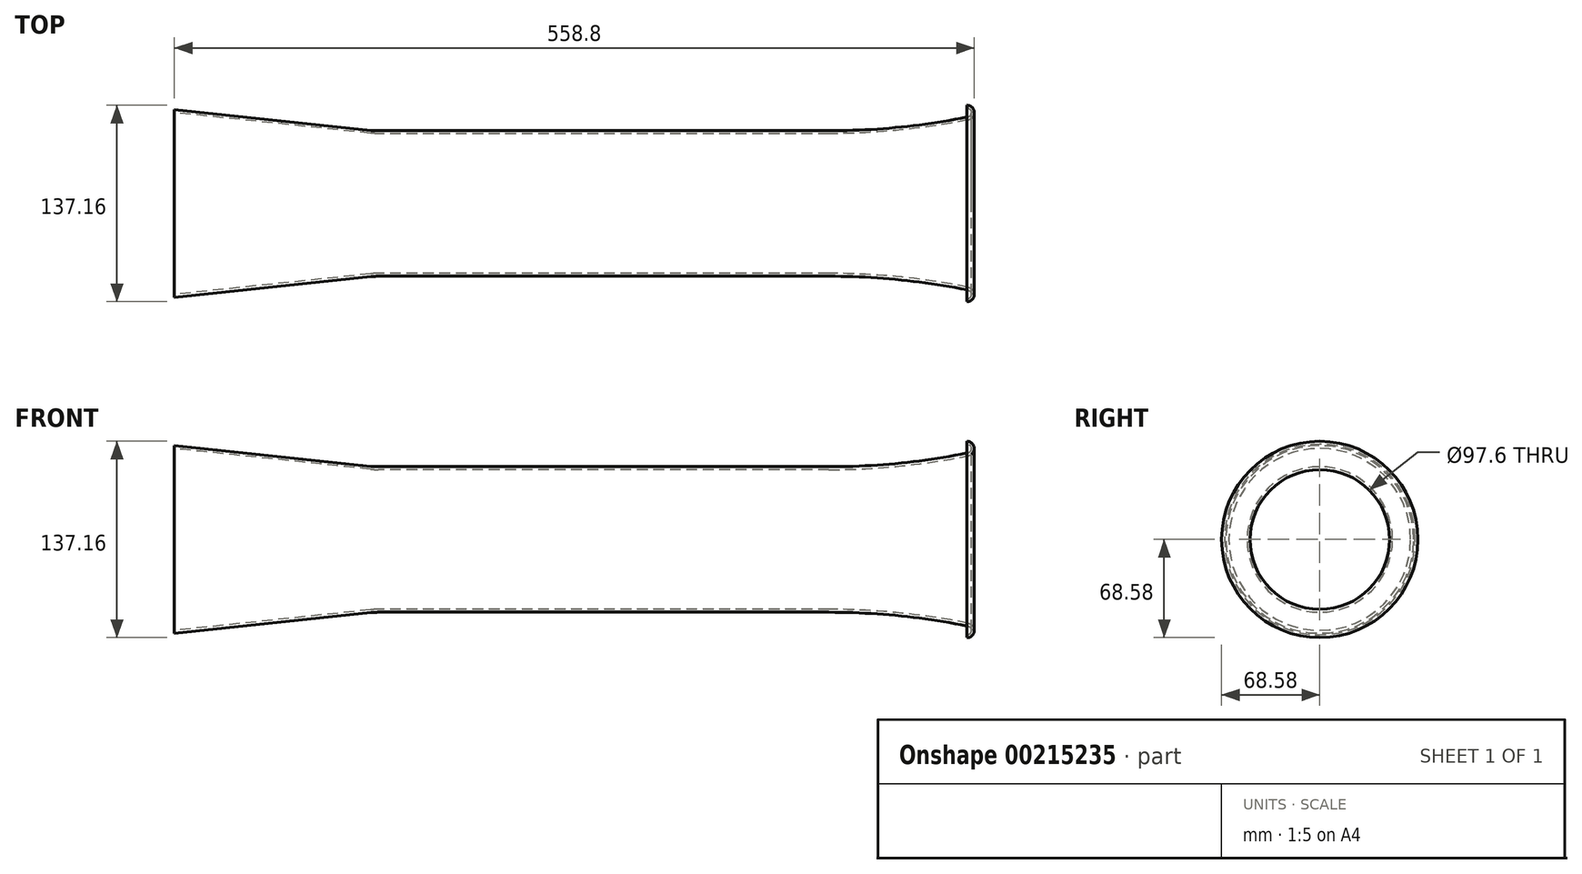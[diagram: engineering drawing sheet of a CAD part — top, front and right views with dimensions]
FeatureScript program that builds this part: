
annotation { "Feature Type Name" : "Feature", "Feature Type Description" : "" }
export const myFeature = defineFeature(function(context is Context, id is Id, definition is map)
    precondition{}
    {
        {
            var Q0;
            Q0=qCreatedBy(makeId("Front.planeOp"),FACE);
            var sketch = newSketch(context, id + "F0", { "sketchPlane" : qUnion([Q0])});
            skLineSegment(sketch, "E0", {"start": v(142.7, 50.8) * mm, "end": v(457.2, 50.8) * mm});
            skLineSegment(sketch, "E1", {"start": v(0, 0) * mm, "end": v(121.25, 0) * mm, "construction": true});
            skLineSegment(sketch, "E2", {"start": v(142.52, 48.8) * mm, "end": v(457.2, 48.8) * mm});
            skLineSegment(sketch, "E3", {"start": v(558.8, 83.35) * mm, "end": v(558.8, 61.17) * mm, "construction": true});
            skLineSegment(sketch, "E4", {"start": v(523.52, 38.1) * mm, "end": v(568, 38.1) * mm, "construction": true});
            skLineSegment(sketch, "E5", {"start": v(553.72, 66.58) * mm, "end": v(553.72, 68.58) * mm});
            skLineSegment(sketch, "E6", {"start": v(0, 65.52) * mm, "end": v(137.38, 51.08) * mm});
            skLineSegment(sketch, "E7", {"start": v(140.03, 50.8) * mm, "end": v(139.86, 48.8) * mm});
            skLineSegment(sketch, "E8", {"start": v(137.21, 49.08) * mm, "end": v(0, 63.5) * mm});
            skLineSegment(sketch, "E9", {"start": v(0, 63.5) * mm, "end": v(0, 65.52) * mm});
            skPoint(sketch, "E10.end.orphan", {"position": v(0, 48.8) * mm});
            skPoint(sketch, "E11.orphan", {"position": v(0, 50.8) * mm});
            skPoint(sketch, "E12.visualSharp", {"position": v(140.03, 50.8) * mm});
            skArc(sketch, "E12.filletArc", {"start": v(137.38, 51.08) * mm, "mid": v(140.03, 50.87) * mm, "end": v(142.7, 50.8) * mm});
            skPoint(sketch, "E13.visualSharp", {"position": v(139.86, 48.8) * mm});
            skArc(sketch, "E13.filletArc", {"start": v(137.21, 49.08) * mm, "mid": v(139.86, 48.87) * mm, "end": v(142.52, 48.8) * mm});
            skArc(sketch, "E14", {"start": v(554.72, 58.52) * mm, "mid": v(558.77, 64) * mm, "end": v(553.72, 68.58) * mm});
            skArc(sketch, "E15", {"start": v(554.33, 60.48) * mm, "mid": v(556.78, 63.8) * mm, "end": v(553.72, 66.58) * mm});
            skArc(sketch, "E16", {"start": v(457.2, 48.8) * mm, "mid": v(506.2, 51.24) * mm, "end": v(554.72, 58.52) * mm});
            skArc(sketch, "E17", {"start": v(457.2, 50.8) * mm, "mid": v(506, 53.23) * mm, "end": v(554.33, 60.48) * mm});
            skSolve(sketch);
        }
        {
            var Q0;
            Q0=qSketchRegion(id+"F0",true);
            var Q1;
            Q1=sQuery(id+"F0.wireOp",EDGE,"E1");
            revolve(context, id + "F1", {"entities" : qUnion([Q0]), "axis" : qUnion([Q1]), "revolveType" : RevolveType.FULL});
        }
    });
